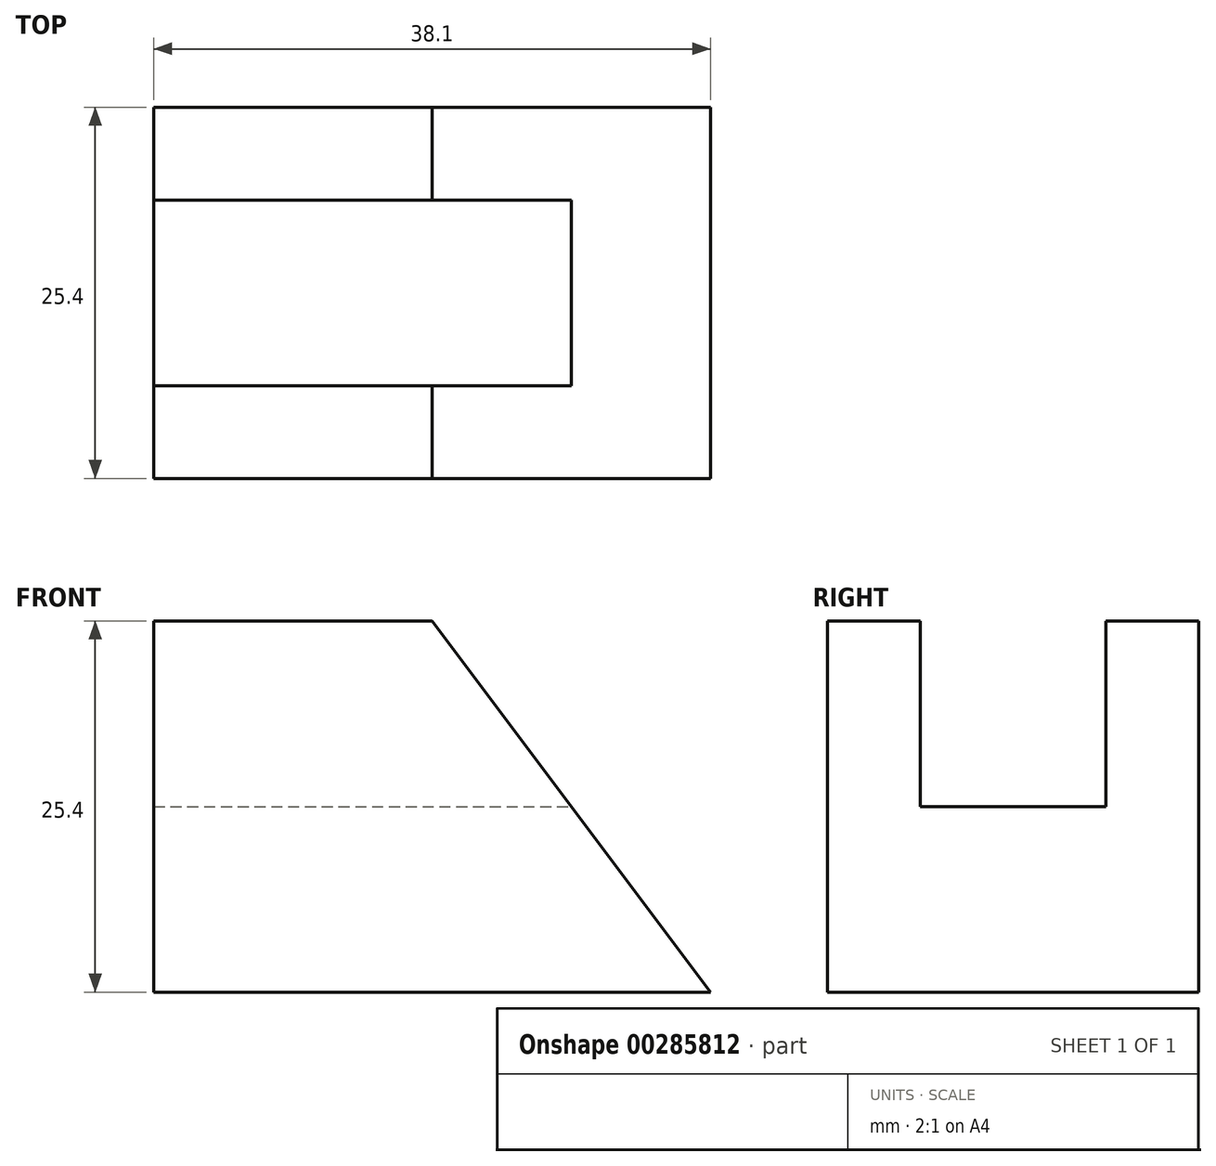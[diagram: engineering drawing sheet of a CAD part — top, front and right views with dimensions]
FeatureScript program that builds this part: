
annotation { "Feature Type Name" : "Feature", "Feature Type Description" : "" }
export const myFeature = defineFeature(function(context is Context, id is Id, definition is map)
    precondition{}
    {
        {
            var Q0;
            Q0=qCreatedBy(makeId("Front.planeOp"),FACE);
            var sketch = newSketch(context, id + "F0", { "sketchPlane" : qUnion([Q0])});
            skLineSegment(sketch, "E0", {"start": v(0, 0) * mm, "end": v(0, 25.4) * mm});
            skLineSegment(sketch, "E1", {"start": v(0, 25.4) * mm, "end": v(19.05, 25.4) * mm});
            skLineSegment(sketch, "E2", {"start": v(19.05, 25.4) * mm, "end": v(38.1, 0) * mm});
            skLineSegment(sketch, "E3", {"start": v(38.1, 0) * mm, "end": v(0, 0) * mm});
            skSolve(sketch);
        }
        {
            var Q0;
            Q0=makeQuery(id+"F0.imprint","IMPRINT",FACE,{"disambiguationData":[TD([[makeQuery(id+"F0.imprint","IMPRINT",EDGE,{"derivedFrom":sQuery(id+"F0.wireOp",EDGE,"E0")}),-1.0]])]});
            extrude(context, id + "F1", {"entities" : qUnion([Q0]), "depth" : 25.4 * mm, "symmetric" : true});
        }
        {
            var Q0;
            Q0=makeQuery(id+"F1.opExtrude","SWEPT_FACE",FACE,{"disambiguationData":[OSD([sQuery(id+"F0.wireOp",EDGE,"E1")])]});
            var sketch = newSketch(context, id + "F2", { "sketchPlane" : qUnion([Q0])});
            skLineSegment(sketch, "E4", {"start": v(0, 6.35) * mm, "end": v(19.05, 6.35) * mm});
            skLineSegment(sketch, "E5", {"start": v(0, -6.35) * mm, "end": v(19.05, -6.35) * mm});
            skSolve(sketch);
        }
        {
            var Q0;
            {var subQ0=sQuery(id+"F2.wireOp",EDGE,"E4");Q0=makeQuery(id+"F2.imprint","IMPRINT",FACE,{"disambiguationData":[TD([[makeQuery(id+"F2.imprint","IMPRINT",EDGE,{"derivedFrom":subQ0}),-1.0]])]});}
            extrude(context, id + "F3", {"entities" : qUnion([Q0]), "operationType" : NewBodyOperationType.REMOVE, "oppositeDirection" : true, "depth" : 12.7 * mm});
        }
        {
            var Q0;
            Q0=makeQuery(id+"F3.boolean.opBoolean","COPY",FACE,{"derivedFrom":makeQuery(id+"F3.opExtrude","SWEPT_FACE",FACE,{"disambiguationData":[OSD([sQuery(id+"F0.wireOp",EDGE,"E1"),sQuery(id+"F0.wireOp",EDGE,"E2")])]})});
            extrude(context, id + "F4", {"entities" : qUnion([Q0]), "operationType" : NewBodyOperationType.REMOVE, "oppositeDirection" : true, "depth" : 25.4 * mm});
        }
    });
